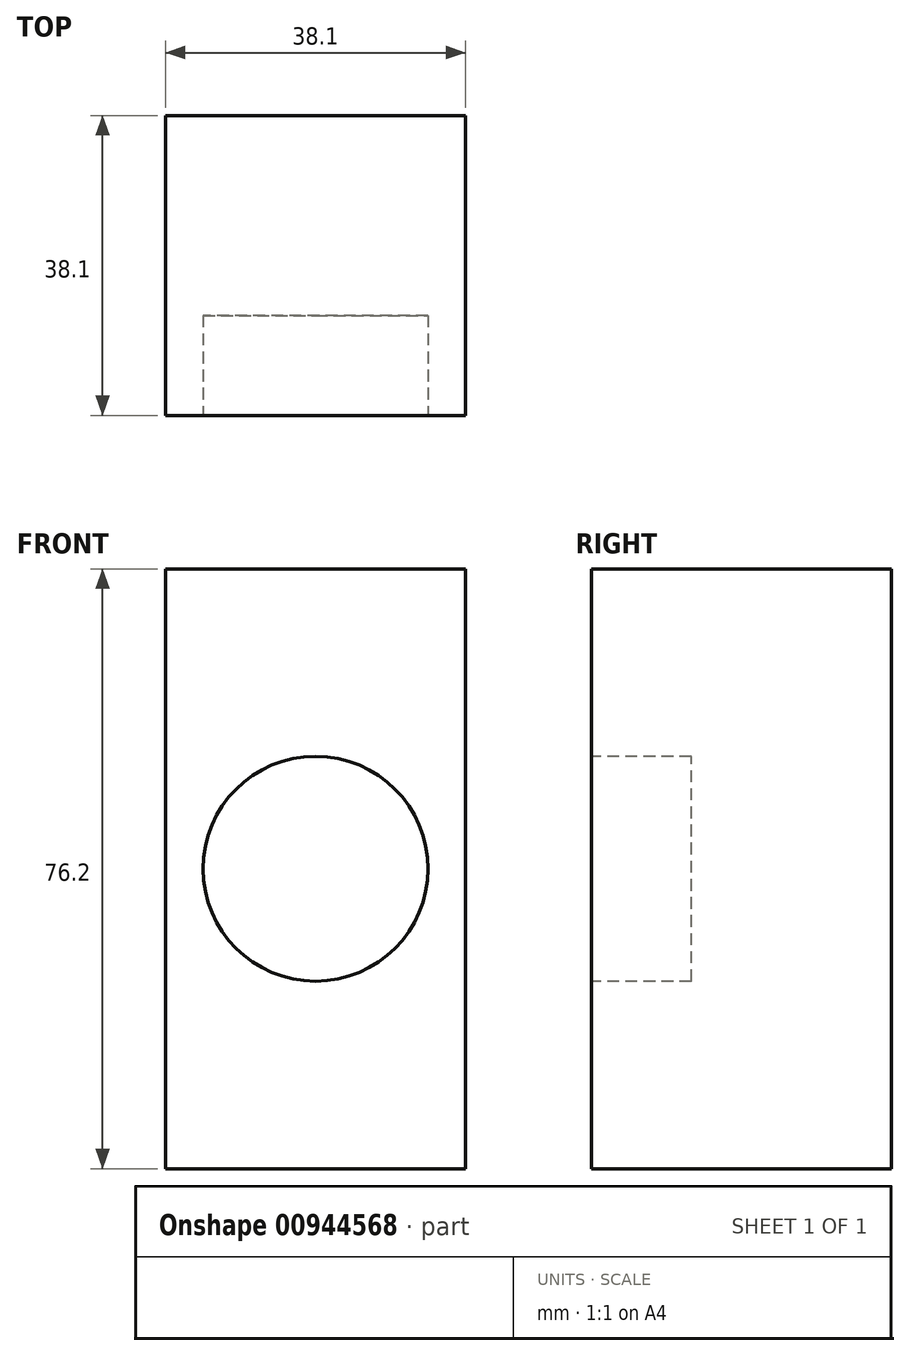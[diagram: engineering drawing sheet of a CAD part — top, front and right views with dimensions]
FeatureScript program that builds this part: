
annotation { "Feature Type Name" : "Feature", "Feature Type Description" : "" }
export const myFeature = defineFeature(function(context is Context, id is Id, definition is map)
    precondition{}
    {
        {
            var Q0;
            Q0=qCreatedBy(makeId("Top.planeOp"),FACE);
            var sketch = newSketch(context, id + "F0", { "sketchPlane" : qUnion([Q0])});
            skLineSegment(sketch, "E0.bottom", {"start": v(0, 0) * mm, "end": v(38.1, 0) * mm});
            skLineSegment(sketch, "E0.top", {"start": v(0, 38.1) * mm, "end": v(38.1, 38.1) * mm});
            skLineSegment(sketch, "E0.left", {"start": v(0, 0) * mm, "end": v(0, 38.1) * mm});
            skLineSegment(sketch, "E0.right", {"start": v(38.1, 0) * mm, "end": v(38.1, 38.1) * mm});
            skSolve(sketch);
        }
        {
            var Q0;
            Q0=makeQuery(id+"F0.imprint","IMPRINT",FACE,{"disambiguationData":[TD([[makeQuery(id+"F0.imprint","IMPRINT",EDGE,{"derivedFrom":sQuery(id+"F0.wireOp",EDGE,"E0.bottom")}),1.0]])]});
            extrude(context, id + "F1", {"entities" : qUnion([Q0]), "depth" : 76.2 * mm, "offsetDistance" : 25.4 * mm});
        }
        {
            var Q0;
            Q0=makeQuery(id+"F1.opExtrude","SWEPT_FACE",FACE,{"disambiguationData":[OSD([sQuery(id+"F0.wireOp",EDGE,"E0.bottom")])]});
            var sketch = newSketch(context, id + "F2", { "sketchPlane" : qUnion([Q0])});
            skLineSegment(sketch, "E1", {"start": v(19.05, 76.2) * mm, "end": v(19.05, 0) * mm, "construction": true});
            skLineSegment(sketch, "E2", {"start": v(0, 38.1) * mm, "end": v(38.1, 38.1) * mm, "construction": true});
            skCircle(sketch, "E3", {"center": v(19.05, 38.1) * mm, "radius": 14.29 * mm});
            skSolve(sketch);
        }
        {
            var Q0;
            Q0 = qSketchRegion(id + "F2", true);
            extrude(context, id + "F3", {"entities" : qUnion([Q0]), "operationType" : NewBodyOperationType.REMOVE, "oppositeDirection" : true, "depth" : 12.7 * mm, "offsetDistance" : 25.4 * mm});
        }
    });
